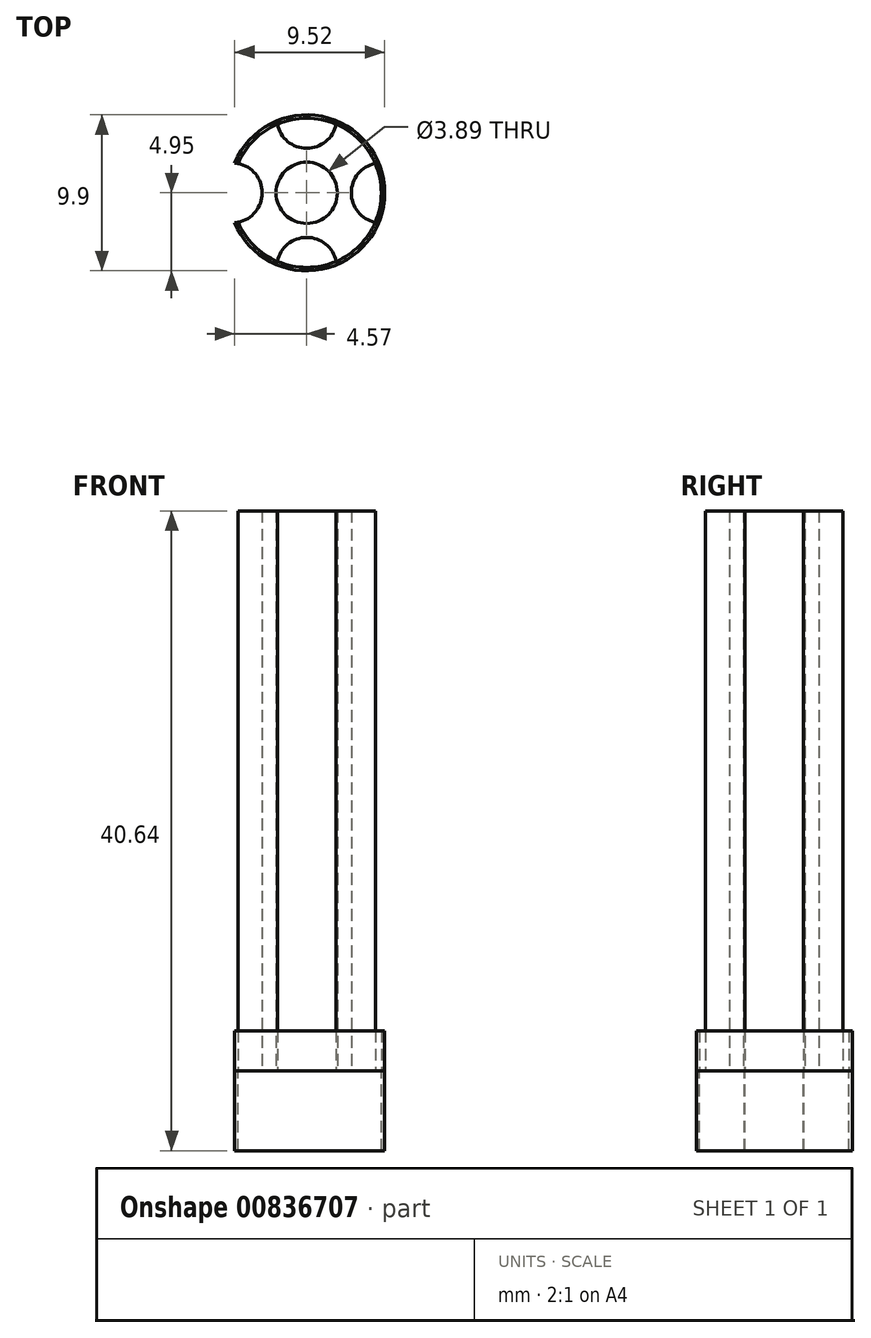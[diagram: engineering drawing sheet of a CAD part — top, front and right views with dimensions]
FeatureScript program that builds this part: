
annotation { "Feature Type Name" : "Feature", "Feature Type Description" : "" }
export const myFeature = defineFeature(function(context is Context, id is Id, definition is map)
    precondition{}
    {
        {
            var Q0;
            Q0=qCreatedBy(makeId("Top.planeOp"),FACE);
            var sketch = newSketch(context, id + "F0", { "sketchPlane" : qUnion([Q0])});
            skCircle(sketch, "E0", {"center": v(0, 0) * mm, "radius": 1.94 * mm});
            skCircle(sketch, "E1", {"center": v(0, 0) * mm, "radius": 4.95 * mm});
            skCircle(sketch, "E2", {"center": v(0, 0) * mm, "radius": 4.74 * mm});
            skArc(sketch, "E3", {"start": v(-1.9, 4.57) * mm, "mid": v(0, 2.83) * mm, "end": v(1.9, 4.57) * mm});
            skArc(sketch, "E4", {"start": v(4.57, 1.9) * mm, "mid": v(2.83, 0) * mm, "end": v(4.57, -1.9) * mm});
            skArc(sketch, "E5", {"start": v(1.9, -4.57) * mm, "mid": v(0, -2.83) * mm, "end": v(-1.9, -4.57) * mm});
            skArc(sketch, "E6", {"start": v(-4.57, -1.9) * mm, "mid": v(-2.83, 0) * mm, "end": v(-4.57, 1.9) * mm});
            skSolve(sketch);
        }
        {
            var Q0;
            {var subQ0=sQuery(id+"F0.wireOp",EDGE,"E3");var subQ1=sQuery(id+"F0.wireOp",EDGE,"E1");var subQ2=makeQuery(id+"F0.imprint","INTERSECT",VERTEX,{"disambiguationData":[OD(0.0)],"derivedFrom":[subQ1,subQ0]});Q0=makeQuery(id+"F0.imprint","IMPRINT",FACE,{"disambiguationData":[TD([[makeQuery(id+"F0.imprint","IMPRINT",EDGE,{"disambiguationData":[TD([[subQ2,-1.0]])],"derivedFrom":subQ1}),1.0]])]});}
            var Q1;
            {var subQ0=sQuery(id+"F0.wireOp",EDGE,"E3");var subQ1=sQuery(id+"F0.wireOp",EDGE,"E1");var subQ2=makeQuery(id+"F0.imprint","INTERSECT",VERTEX,{"disambiguationData":[OD(0.0)],"derivedFrom":[subQ1,subQ0]});Q1=makeQuery(id+"F0.imprint","IMPRINT",FACE,{"disambiguationData":[TD([[makeQuery(id+"F0.imprint","IMPRINT",EDGE,{"disambiguationData":[TD([[subQ2,1.0]])],"derivedFrom":subQ1}),1.0]])]});}
            var Q2;
            {var subQ0=sQuery(id+"F0.wireOp",EDGE,"E3");var subQ1=sQuery(id+"F0.wireOp",EDGE,"E1");var subQ2=makeQuery(id+"F0.imprint","INTERSECT",VERTEX,{"disambiguationData":[OD(1.0)],"derivedFrom":[subQ1,subQ0]});Q2=makeQuery(id+"F0.imprint","IMPRINT",FACE,{"disambiguationData":[TD([[makeQuery(id+"F0.imprint","IMPRINT",EDGE,{"disambiguationData":[TD([[subQ2,1.0]])],"derivedFrom":subQ1}),1.0]])]});}
            var Q3;
            {var subQ0=sQuery(id+"F0.wireOp",EDGE,"E4");var subQ1=sQuery(id+"F0.wireOp",EDGE,"E1");var subQ2=makeQuery(id+"F0.imprint","INTERSECT",VERTEX,{"disambiguationData":[OD(0.0)],"derivedFrom":[subQ1,subQ0]});Q3=makeQuery(id+"F0.imprint","IMPRINT",FACE,{"disambiguationData":[TD([[makeQuery(id+"F0.imprint","IMPRINT",EDGE,{"disambiguationData":[TD([[subQ2,1.0]])],"derivedFrom":subQ1}),1.0]])]});}
            var Q4;
            {var subQ0=sQuery(id+"F0.wireOp",EDGE,"E4");var subQ1=sQuery(id+"F0.wireOp",EDGE,"E1");var subQ2=makeQuery(id+"F0.imprint","INTERSECT",VERTEX,{"disambiguationData":[OD(1.0)],"derivedFrom":[subQ1,subQ0]});Q4=makeQuery(id+"F0.imprint","IMPRINT",FACE,{"disambiguationData":[TD([[makeQuery(id+"F0.imprint","IMPRINT",EDGE,{"disambiguationData":[TD([[subQ2,1.0]])],"derivedFrom":subQ1}),1.0]])]});}
            var Q5;
            {var subQ0=sQuery(id+"F0.wireOp",EDGE,"E5");var subQ1=sQuery(id+"F0.wireOp",EDGE,"E1");var subQ2=makeQuery(id+"F0.imprint","INTERSECT",VERTEX,{"disambiguationData":[OD(0.0)],"derivedFrom":[subQ1,subQ0]});Q5=makeQuery(id+"F0.imprint","IMPRINT",FACE,{"disambiguationData":[TD([[makeQuery(id+"F0.imprint","IMPRINT",EDGE,{"disambiguationData":[TD([[subQ2,1.0]])],"derivedFrom":subQ1}),1.0]])]});}
            var Q6;
            {var subQ0=sQuery(id+"F0.wireOp",EDGE,"E5");var subQ1=sQuery(id+"F0.wireOp",EDGE,"E1");var subQ2=makeQuery(id+"F0.imprint","INTERSECT",VERTEX,{"disambiguationData":[OD(1.0)],"derivedFrom":[subQ1,subQ0]});Q6=makeQuery(id+"F0.imprint","IMPRINT",FACE,{"disambiguationData":[TD([[makeQuery(id+"F0.imprint","IMPRINT",EDGE,{"disambiguationData":[TD([[subQ2,1.0]])],"derivedFrom":subQ1}),1.0]])]});}
            var Q7;
            {var subQ0=sQuery(id+"F0.wireOp",EDGE,"E6");var subQ1=sQuery(id+"F0.wireOp",EDGE,"E1");var subQ2=makeQuery(id+"F0.imprint","INTERSECT",VERTEX,{"disambiguationData":[OD(0.0)],"derivedFrom":[subQ1,subQ0]});Q7=makeQuery(id+"F0.imprint","IMPRINT",FACE,{"disambiguationData":[TD([[makeQuery(id+"F0.imprint","IMPRINT",EDGE,{"disambiguationData":[TD([[subQ2,1.0]])],"derivedFrom":subQ1}),1.0]])]});}
            extrude(context, id + "F1", {"entities" : qUnion([Q0, Q1, Q2, Q3, Q4, Q5, Q6, Q7]), "depth" : -5.08 * mm, "offsetDistance" : 25.4 * mm});
        }
        {
            var Q0;
            Q0=makeQuery(id+"F0.imprint","IMPRINT",FACE,{"disambiguationData":[TD([[makeQuery(id+"F0.imprint","IMPRINT",EDGE,{"derivedFrom":sQuery(id+"F0.wireOp",EDGE,"E0")}),-1.0]])]});
            extrude(context, id + "F2", {"entities" : qUnion([Q0]), "depth" : 35.56 * mm, "offsetDistance" : 25.4 * mm});
        }
        {
            var Q0;
            {var subQ0=sQuery(id+"F0.wireOp",EDGE,"E5");var subQ1=sQuery(id+"F0.wireOp",EDGE,"E1");var subQ2=makeQuery(id+"F0.imprint","INTERSECT",VERTEX,{"disambiguationData":[OD(0.0)],"derivedFrom":[subQ1,subQ0]});Q0=makeQuery(id+"F0.imprint","IMPRINT",FACE,{"disambiguationData":[TD([[makeQuery(id+"F0.imprint","IMPRINT",EDGE,{"disambiguationData":[TD([[subQ2,1.0]])],"derivedFrom":subQ1}),1.0]])]});}
            var Q1;
            {var subQ0=sQuery(id+"F0.wireOp",EDGE,"E4");var subQ1=sQuery(id+"F0.wireOp",EDGE,"E1");var subQ2=makeQuery(id+"F0.imprint","INTERSECT",VERTEX,{"disambiguationData":[OD(1.0)],"derivedFrom":[subQ1,subQ0]});Q1=makeQuery(id+"F0.imprint","IMPRINT",FACE,{"disambiguationData":[TD([[makeQuery(id+"F0.imprint","IMPRINT",EDGE,{"disambiguationData":[TD([[subQ2,1.0]])],"derivedFrom":subQ1}),1.0]])]});}
            var Q2;
            {var subQ0=sQuery(id+"F0.wireOp",EDGE,"E4");var subQ1=sQuery(id+"F0.wireOp",EDGE,"E1");var subQ2=makeQuery(id+"F0.imprint","INTERSECT",VERTEX,{"disambiguationData":[OD(0.0)],"derivedFrom":[subQ1,subQ0]});Q2=makeQuery(id+"F0.imprint","IMPRINT",FACE,{"disambiguationData":[TD([[makeQuery(id+"F0.imprint","IMPRINT",EDGE,{"disambiguationData":[TD([[subQ2,1.0]])],"derivedFrom":subQ1}),1.0]])]});}
            var Q3;
            {var subQ0=sQuery(id+"F0.wireOp",EDGE,"E3");var subQ1=sQuery(id+"F0.wireOp",EDGE,"E1");var subQ2=makeQuery(id+"F0.imprint","INTERSECT",VERTEX,{"disambiguationData":[OD(1.0)],"derivedFrom":[subQ1,subQ0]});Q3=makeQuery(id+"F0.imprint","IMPRINT",FACE,{"disambiguationData":[TD([[makeQuery(id+"F0.imprint","IMPRINT",EDGE,{"disambiguationData":[TD([[subQ2,1.0]])],"derivedFrom":subQ1}),1.0]])]});}
            var Q4;
            {var subQ0=sQuery(id+"F0.wireOp",EDGE,"E3");var subQ1=sQuery(id+"F0.wireOp",EDGE,"E1");var subQ2=makeQuery(id+"F0.imprint","INTERSECT",VERTEX,{"disambiguationData":[OD(0.0)],"derivedFrom":[subQ1,subQ0]});Q4=makeQuery(id+"F0.imprint","IMPRINT",FACE,{"disambiguationData":[TD([[makeQuery(id+"F0.imprint","IMPRINT",EDGE,{"disambiguationData":[TD([[subQ2,1.0]])],"derivedFrom":subQ1}),1.0]])]});}
            var Q5;
            {var subQ0=sQuery(id+"F0.wireOp",EDGE,"E3");var subQ1=sQuery(id+"F0.wireOp",EDGE,"E1");var subQ2=makeQuery(id+"F0.imprint","INTERSECT",VERTEX,{"disambiguationData":[OD(0.0)],"derivedFrom":[subQ1,subQ0]});Q5=makeQuery(id+"F0.imprint","IMPRINT",FACE,{"disambiguationData":[TD([[makeQuery(id+"F0.imprint","IMPRINT",EDGE,{"disambiguationData":[TD([[subQ2,-1.0]])],"derivedFrom":subQ1}),1.0]])]});}
            var Q6;
            {var subQ0=sQuery(id+"F0.wireOp",EDGE,"E6");var subQ1=sQuery(id+"F0.wireOp",EDGE,"E1");var subQ2=makeQuery(id+"F0.imprint","INTERSECT",VERTEX,{"disambiguationData":[OD(0.0)],"derivedFrom":[subQ1,subQ0]});Q6=makeQuery(id+"F0.imprint","IMPRINT",FACE,{"disambiguationData":[TD([[makeQuery(id+"F0.imprint","IMPRINT",EDGE,{"disambiguationData":[TD([[subQ2,1.0]])],"derivedFrom":subQ1}),1.0]])]});}
            var Q7;
            {var subQ0=sQuery(id+"F0.wireOp",EDGE,"E5");var subQ1=sQuery(id+"F0.wireOp",EDGE,"E1");var subQ2=makeQuery(id+"F0.imprint","INTERSECT",VERTEX,{"disambiguationData":[OD(1.0)],"derivedFrom":[subQ1,subQ0]});Q7=makeQuery(id+"F0.imprint","IMPRINT",FACE,{"disambiguationData":[TD([[makeQuery(id+"F0.imprint","IMPRINT",EDGE,{"disambiguationData":[TD([[subQ2,1.0]])],"derivedFrom":subQ1}),1.0]])]});}
            extrude(context, id + "F3", {"entities" : qUnion([Q0, Q1, Q2, Q3, Q4, Q5, Q6, Q7]), "depth" : 2.54 * mm, "offsetDistance" : 25.4 * mm});
        }
    });
